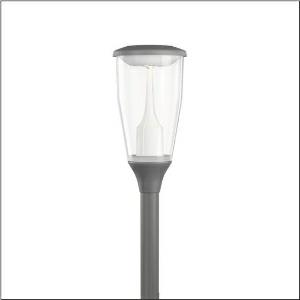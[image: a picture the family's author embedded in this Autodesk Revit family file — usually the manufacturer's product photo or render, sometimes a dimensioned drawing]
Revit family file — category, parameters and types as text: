
# Revit family: dl_11_iq___p1_0a_5xa5575bf14h000022_7e97
name_source: partatom
category: Lighting Fixtures
units: mm (PartAtom-declared; Revit-internal decimal feet)

## family parameters
Cut with Voids When Loaded = No
Host = Face
Light Source = No
Part Type = Normal
Room Calculation Point = No
Round Connector Dimension = Use Diameter
Shared = No

## types (1)
- --- (1 x LED, 1530 lm, 12.9 W, 2200K)
    Apparent Load = 13 VA
    CIE Flux Codes = 34 63 91 95 100
    Color Rendering = 70
    Color Temperature = 2200K
    Default Elevation = 1800 mm
    Description = DL 11 iQ, mast luminaire, Module 540 iQ-SR, primary light control with 3 zone facetted reflector, of plastic, silver coated, highly specular, structured, primary optical cover: cover, of PMMA, transparent, light distribution: P1.0a, light emission: direct distribution, primary light characteristic: asymmetric, installation type: post-top, LED, High Power LED, rated luminous flux: 1.560lm, luminous efficacy: 149lm/W, light colour: 722, colour temperature: 2200K, control gear: iQ Street-Remote, control: Street-Remote, Auto-Match, Temp-Guard, Lumen-Switch, Night-Set, Smart-Wire, Light-Fading, Desk-Remote (wireless, voltage-free reading and setting of iQ features in the workshop via application-optimized NFC function/RFID function), optimised constant luminous flux control (CLO 2.0), mains connection: 220..240V, AC, 50/60Hz, connection cable pre-assembled, cable length: 5,5m, wiring characteristics: H07RN-F, 5-core, 1.5mm², start of lifetime: 13W, end of service life: 13W, reduction: 5W, luminaire housing, upper part, of diecast aluminium, coated, SITECO metallic grey (DB 702S), spigot size: 76mm (post-top), mounting height: 3..5m, post-top mast mounting element, of diecast aluminium, coated, SITECO metallic grey (DB 702S), Module 540 iQ-SR, traffic white (RAL 9016), equipment: standard, protection rating (complete): IP66, insulation class (complete): insulation class II (safety insulation), certification: CE, ENEC, ENEC+, VDE, impact resistance: IK07, packaging unit: 1 piece

Light Distribution: P1.0a
    Height = 665 mm
    Lamp = 1 x LED
    Lamp Light Flux = 1530 lm
    Lamp Power = 12.9 W
    Lamp count = 1
    Length = 334 mm
    Luminous efficacy = 119 lm/W
    Manufacturer = Siteco
    ModVariant = No
    Model = 5XA5575BF14H000022
    Number of Poles = 1
    OnlyDefault = Yes
    Power Factor = 1
    Product Name = DL 11 iQ | P1.0a
    Product group = mast luminaire | pylon top
    ProductGroupID = 6100
    Protection Class = Protection class II
    Protection Degree = IP 66
    RLX_Detail_Level = 1
    RLX_Emergency_Light_Flux = 0 lm
    RLX_Emergency_Type = 0
    RLX_Emergency_Type_DB = No
    RlxData = <blob elided: 104457 chars, md5=9daf07e3>
    Socket = socket
    Standby Power = 0 W
    System Light Flux = 1530 lm
    System Power = 13 W
    Type Comments = factory setting: luminous flux: 100 % | dim-lin: 254 | 516 mA
    Type Image = l_1258354.jpg
    URL = http://relux.com
    VarID = @adj_095647
    Voltage = 0 V
    Weight = 0.00 kg
    Width = 0 mm  [stored 0 ft]

note: [stored X ft] marks values corroborated as IEEE doubles in the binary element streams (Revit-internal decimal feet)

## geometry (parser evidence)
native form markers: Blend x4, Sweep x11
no freeform markers — native parametric forms only
